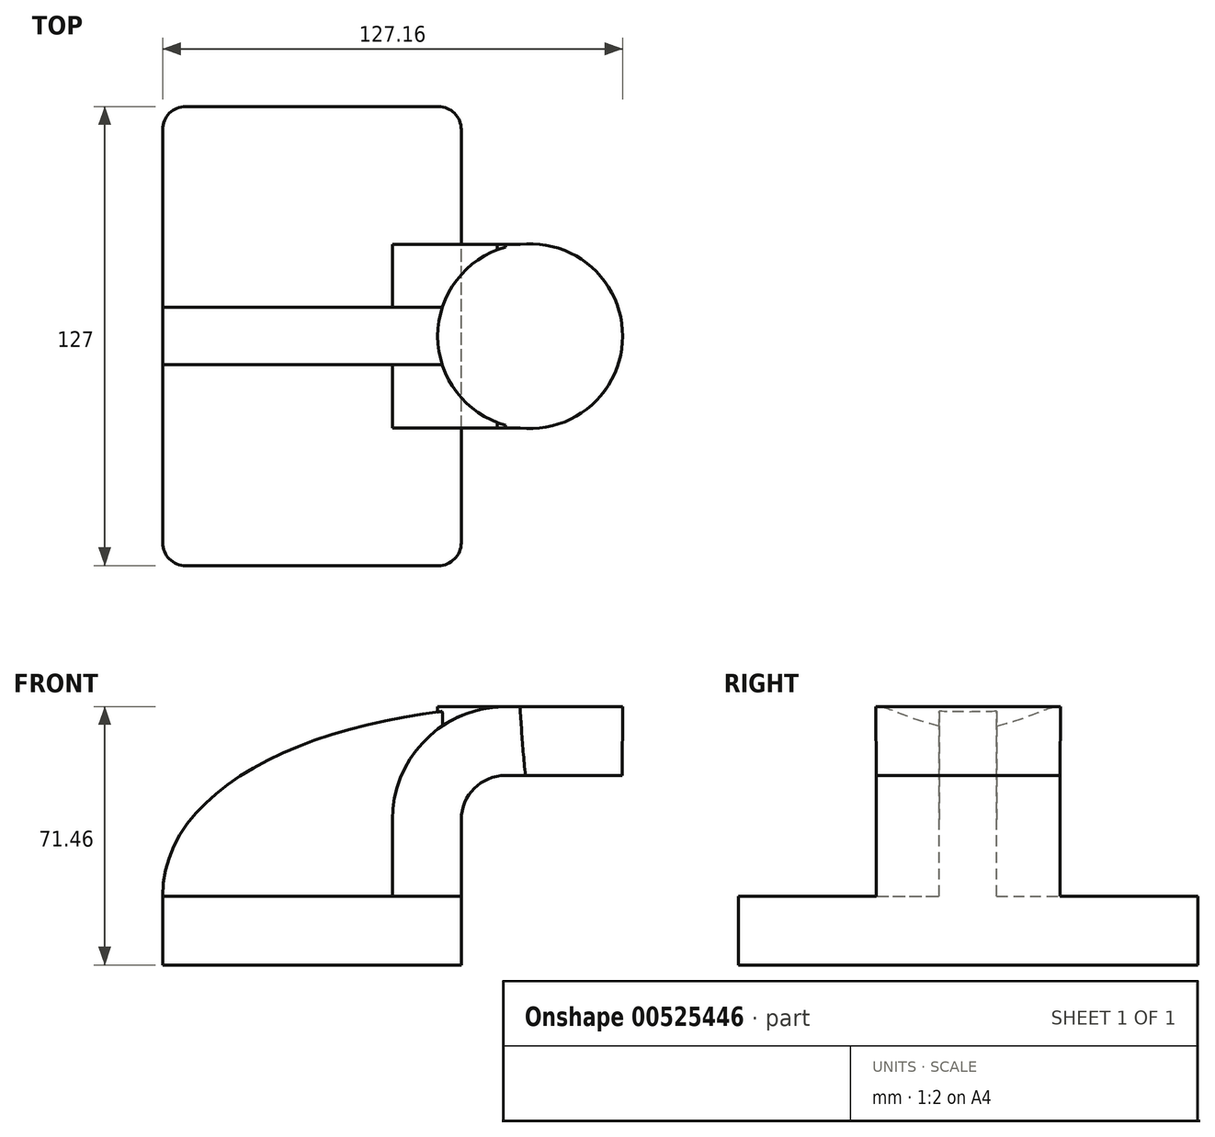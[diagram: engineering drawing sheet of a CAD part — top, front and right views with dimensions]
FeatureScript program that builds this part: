
annotation { "Feature Type Name" : "Feature", "Feature Type Description" : "" }
export const myFeature = defineFeature(function(context is Context, id is Id, definition is map)
    precondition{}
    {
        {
            var Q0;
            Q0=qCreatedBy(makeId("Front.planeOp"),FACE);
            var sketch = newSketch(context, id + "F0", { "sketchPlane" : qUnion([Q0])});
            skLineSegment(sketch, "E0.bottom", {"start": v(-41.28, -9.53) * mm, "end": v(41.28, -9.53) * mm});
            skLineSegment(sketch, "E0.top", {"start": v(-41.28, 9.53) * mm, "end": v(41.28, 9.53) * mm});
            skLineSegment(sketch, "E0.left", {"start": v(-41.28, -9.53) * mm, "end": v(-41.28, 9.53) * mm});
            skLineSegment(sketch, "E0.right", {"start": v(41.28, -9.53) * mm, "end": v(41.28, 9.53) * mm});
            skPoint(sketch, "E0.middle", {"position": v(0, 0) * mm});
            skLineSegment(sketch, "E1.bottom", {"start": v(60.33, 38.1) * mm, "end": v(111.13, 38.1) * mm});
            skLineSegment(sketch, "E1.top", {"start": v(60.33, 66.67) * mm, "end": v(111.13, 66.67) * mm});
            skLineSegment(sketch, "E1.left", {"start": v(60.33, 38.1) * mm, "end": v(60.33, 66.67) * mm});
            skLineSegment(sketch, "E1.right", {"start": v(111.13, 38.1) * mm, "end": v(111.13, 66.67) * mm});
            skPoint(sketch, "E1.middle", {"position": v(85.73, 52.39) * mm});
            skLineSegment(sketch, "E2", {"start": v(41.28, 9.53) * mm, "end": v(41.28, 30.65) * mm});
            skArc(sketch, "E3", {"start": v(41.27, 30.65) * mm, "mid": v(44.86, 39.3) * mm, "end": v(53.5, 42.88) * mm});
            skLineSegment(sketch, "E4", {"start": v(53.5, 42.88) * mm, "end": v(85.9, 42.88) * mm});
            skLineSegment(sketch, "E5.0", {"start": v(53.5, 61.93) * mm, "end": v(85.9, 61.93) * mm});
            skArc(sketch, "E5.1", {"start": v(22.22, 30.65) * mm, "mid": v(31.39, 52.76) * mm, "end": v(53.5, 61.93) * mm});
            skLineSegment(sketch, "E5.2", {"start": v(22.22, 9.53) * mm, "end": v(22.22, 30.65) * mm});
            skLineSegment(sketch, "E6", {"start": v(85.73, 38.1) * mm, "end": v(85.9, 66.67) * mm});
            skFitSpline(sketch, "E7", {"points": [v(-41.28, 9.53) * mm, v(53.5, 61.93) * mm], "startDerivative": vector(-0.1, 96.82) * mm, "endDerivative": vector(143.28, 4.4) * mm});
            skSolve(sketch);
        }
        {
            var Q0;
            Q0=makeQuery(id+"F0.imprint","IMPRINT",FACE,{"disambiguationData":[TD([[makeQuery(id+"F0.imprint","IMPRINT",EDGE,{"derivedFrom":sQuery(id+"F0.wireOp",EDGE,"E0.bottom")}),1.0]])]});
            extrude(context, id + "F1", {"entities" : qUnion([Q0]), "endBound" : BoundingType.SYMMETRIC, "depth" : 127 * mm, "offsetDistance" : 25.4 * mm});
        }
        {
            var Q0;
            {var subQ1=sQuery(id+"F0.wireOp",EDGE,"E2");Q0=makeQuery(id+"F0.imprint","IMPRINT",FACE,{"disambiguationData":[TD([[makeQuery(id+"F0.imprint","IMPRINT",EDGE,{"derivedFrom":subQ1}),1.0]])]});}
            extrude(context, id + "F2", {"entities" : qUnion([Q0]), "operationType" : NewBodyOperationType.ADD, "endBound" : BoundingType.SYMMETRIC, "depth" : 50.8 * mm, "offsetDistance" : 25.4 * mm});
        }
        {
            var Q0;
            {var subQ3=sQuery(id+"F0.wireOp",EDGE,"E5.2");Q0=makeQuery(id+"F0.imprint","IMPRINT",FACE,{"disambiguationData":[TD([[makeQuery(id+"F0.imprint","IMPRINT",EDGE,{"derivedFrom":subQ3}),1.0]])]});}
            extrude(context, id + "F3", {"entities" : qUnion([Q0]), "operationType" : NewBodyOperationType.ADD, "endBound" : BoundingType.SYMMETRIC, "depth" : 15.88 * mm, "offsetDistance" : 25.4 * mm});
        }
        {
            var Q0;
            {var subQ0=sQuery(id+"F0.wireOp",EDGE,"E4");var subQ1=sQuery(id+"F0.wireOp",EDGE,"E1.left");var subQ2=makeQuery(id+"F0.imprint","INTERSECT",VERTEX,{"derivedFrom":[subQ1,subQ0]});Q0=makeQuery(id+"F0.imprint","IMPRINT",FACE,{"disambiguationData":[TD([[makeQuery(id+"F0.imprint","IMPRINT",EDGE,{"disambiguationData":[TD([[subQ2,-1.0]])],"derivedFrom":subQ1}),-1.0]])]});}
            var Q1;
            Q1=sQuery(id+"F0.wireOp",EDGE,"E1.left");
            revolve(context, id + "F4", {"operationType" : NewBodyOperationType.ADD, "entities" : qUnion([Q0]), "axis" : qUnion([Q1]), "revolveType" : RevolveType.FULL});
        }
        {
            var Q0;
            Q0=makeQuery(id+"F1.opExtrude","CAP_EDGE",EDGE,{"disambiguationData":[OSD([sQuery(id+"F0.wireOp",EDGE,"E0.left")])],"isStart":false});
            var Q1;
            Q1=makeQuery(id+"F1.opExtrude","CAP_EDGE",EDGE,{"disambiguationData":[OSD([sQuery(id+"F0.wireOp",EDGE,"E0.right")])],"isStart":false});
            var Q2;
            Q2=makeQuery(id+"F1.opExtrude","CAP_EDGE",EDGE,{"disambiguationData":[OSD([sQuery(id+"F0.wireOp",EDGE,"E0.right")])],"isStart":true});
            var Q3;
            Q3=makeQuery(id+"F1.opExtrude","CAP_EDGE",EDGE,{"disambiguationData":[OSD([sQuery(id+"F0.wireOp",EDGE,"E0.left")])],"isStart":true});
            fillet(context, id + "F5", {"entities" : qUnion([Q0, Q1, Q2, Q3]), "radius" : 6.35 * mm, "tangentPropagation" : true, "allowEdgeOverflow" : false});
        }
    });
